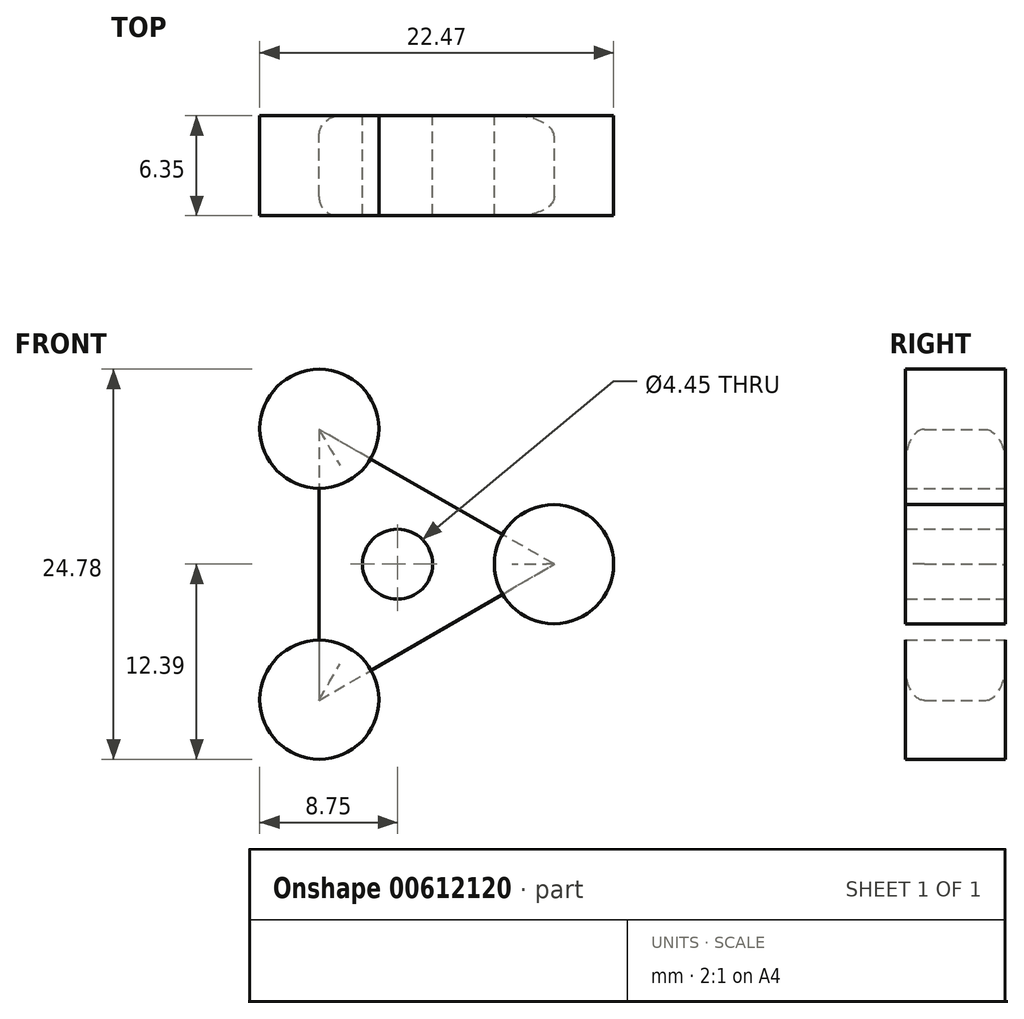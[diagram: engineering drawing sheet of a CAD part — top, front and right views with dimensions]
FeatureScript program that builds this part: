
annotation { "Feature Type Name" : "Feature", "Feature Type Description" : "" }
export const myFeature = defineFeature(function(context is Context, id is Id, definition is map)
    precondition{}
    {
        {
            var Q0;
            Q0=qCreatedBy(makeId("Front.planeOp"),FACE);
            var sketch = newSketch(context, id + "F0", { "sketchPlane" : qUnion([Q0])});
            skCircle(sketch, "E0", {"center": v(9.94, 0) * mm, "radius": 3.79 * mm});
            skCircle(sketch, "E1.1.0", {"center": v(-4.97, 8.6) * mm, "radius": 3.79 * mm});
            skCircle(sketch, "E1.2.0", {"center": v(-4.97, -8.6) * mm, "radius": 3.79 * mm});
            skPoint(sketch, "E1.center", {"position": v(0, 0) * mm});
            skSolve(sketch);
        }
        {
            var Q0;
            Q0=qCreatedBy(makeId("Front.planeOp"),FACE);
            var sketch = newSketch(context, id + "F1", { "sketchPlane" : qUnion([Q0])});
            skLineSegment(sketch, "E2", {"start": v(-5, 8.57) * mm, "end": v(-5, -8.66) * mm});
            skLineSegment(sketch, "E3", {"start": v(-5, -8.66) * mm, "end": v(9.96, 0) * mm});
            skLineSegment(sketch, "E4", {"start": v(9.96, 0) * mm, "end": v(-5, 8.57) * mm});
            skSolve(sketch);
        }
        {
            var Q0;
            Q0 = qSketchRegion(id + "F0", true);
            var Q1;
            Q1 = qSketchRegion(id + "F1", true);
            extrude(context, id + "F2", {"entities" : qUnion([Q0, Q1]), "depth" : 6.35 * mm, "offsetDistance" : 25.4 * mm});
        }
        {
            var Q0;
            Q0=makeQuery(id+"F2.opExtrude","CAP_EDGE",EDGE,{"disambiguationData":[OSD([sQuery(id+"F1.wireOp",EDGE,"E4")])],"isStart":true});
            var Q1;
            Q1=makeQuery(id+"F2.opExtrude","CAP_EDGE",EDGE,{"disambiguationData":[OSD([sQuery(id+"F1.wireOp",EDGE,"E2")])],"isStart":true});
            var Q2;
            Q2=makeQuery(id+"F2.opExtrude","CAP_EDGE",EDGE,{"disambiguationData":[OSD([sQuery(id+"F1.wireOp",EDGE,"E3")])],"isStart":true});
            fillet(context, id + "F3", {"entities" : qUnion([Q0, Q1, Q2]), "radius" : 1.34 * mm, "tangentPropagation" : true, "allowEdgeOverflow" : false});
        }
        {
            var Q0;
            Q0=makeQuery(id+"F2.opExtrude","CAP_EDGE",EDGE,{"disambiguationData":[OSD([sQuery(id+"F1.wireOp",EDGE,"E2")])],"isStart":false});
            var Q1;
            Q1=makeQuery(id+"F2.opExtrude","CAP_EDGE",EDGE,{"disambiguationData":[OSD([sQuery(id+"F1.wireOp",EDGE,"E4")])],"isStart":false});
            var Q2;
            Q2=makeQuery(id+"F2.opExtrude","CAP_EDGE",EDGE,{"disambiguationData":[OSD([sQuery(id+"F1.wireOp",EDGE,"E3")])],"isStart":false});
            fillet(context, id + "F4", {"entities" : qUnion([Q0, Q1, Q2]), "radius" : 1.2 * mm, "tangentPropagation" : true, "allowEdgeOverflow" : false});
        }
        {
            var Q0;
            Q0=sQuery(id+"F0.wireOp",VERTEX,"E1.center");
            var Q1;
            Q1=makeQuery(id+"F2.opExtrude","SWEPT_BODY",BODY,{"disambiguationData":[OSD([sQuery(id+"F1.wireOp",EDGE,"E2"),sQuery(id+"F1.wireOp",EDGE,"E3"),sQuery(id+"F1.wireOp",EDGE,"E4")])]});
            hole(context, id + "F5", {"style" : HoleStyle.SIMPLE, "endStyle" : HoleEndStyle.THROUGH, "oppositeDirection" : true, "holeDiameter" : 4.44 * mm, "majorDiameter" : 6.35 * mm, "isTappedThrough" : true, "tappedDepth" : 12.7 * mm, "tapClearance" : 3, "locations" : qUnion([Q0]), "scope" : qUnion([Q1])});
        }
    });
